# Revit family: Accessory-Sink_Rack-KOHLER-NEOROC_CAIRN-K-27788
name_source: partatom
category: Specialty Equipment
revit_build: Autodesk Revit 2017 (Build: 20160225_1515(x64)
units: mm (PartAtom-declared; Revit-internal decimal feet)

## family parameters
Cut with Voids When Loaded = No
Host = Face
OmniClass Number = 23.31.13.17
Part Type = Normal
Room Calculation Point = No
Round Connector Dimension = Use Diameter
Shared = No

## types (1)
- ST-Stainless Steel
    ADA Compliant = No
    Assembly Code = C1030200
    Date Modified = 12/17/2021
    Default Elevation = 42"
    Description = LAUNDRY SINK UTILITY RACK
    Finish = Kohler-Metal-ST-Stainless_Steel
    Height = 1/4"
    Length = 14 1/4"
    Manufacturer = KOHLER Co.
    MasterFormat 1995 = 10820
    MasterFormat 2004 = 10.28.13
    Material = Stainless Steel
    Model = K-27788-ST
    Product Documentation Link = https://www.us.kohler.com
    Product Name = NEOROC CAIRN
    Product Page URL = http://www.us.kohler.com
    URL = https://www.us.kohler.com
    WaterSense Certified = No
    Width = 8 3/8"

## geometry (parser evidence)
native form markers: Sweep x6
no freeform markers — native parametric forms only
